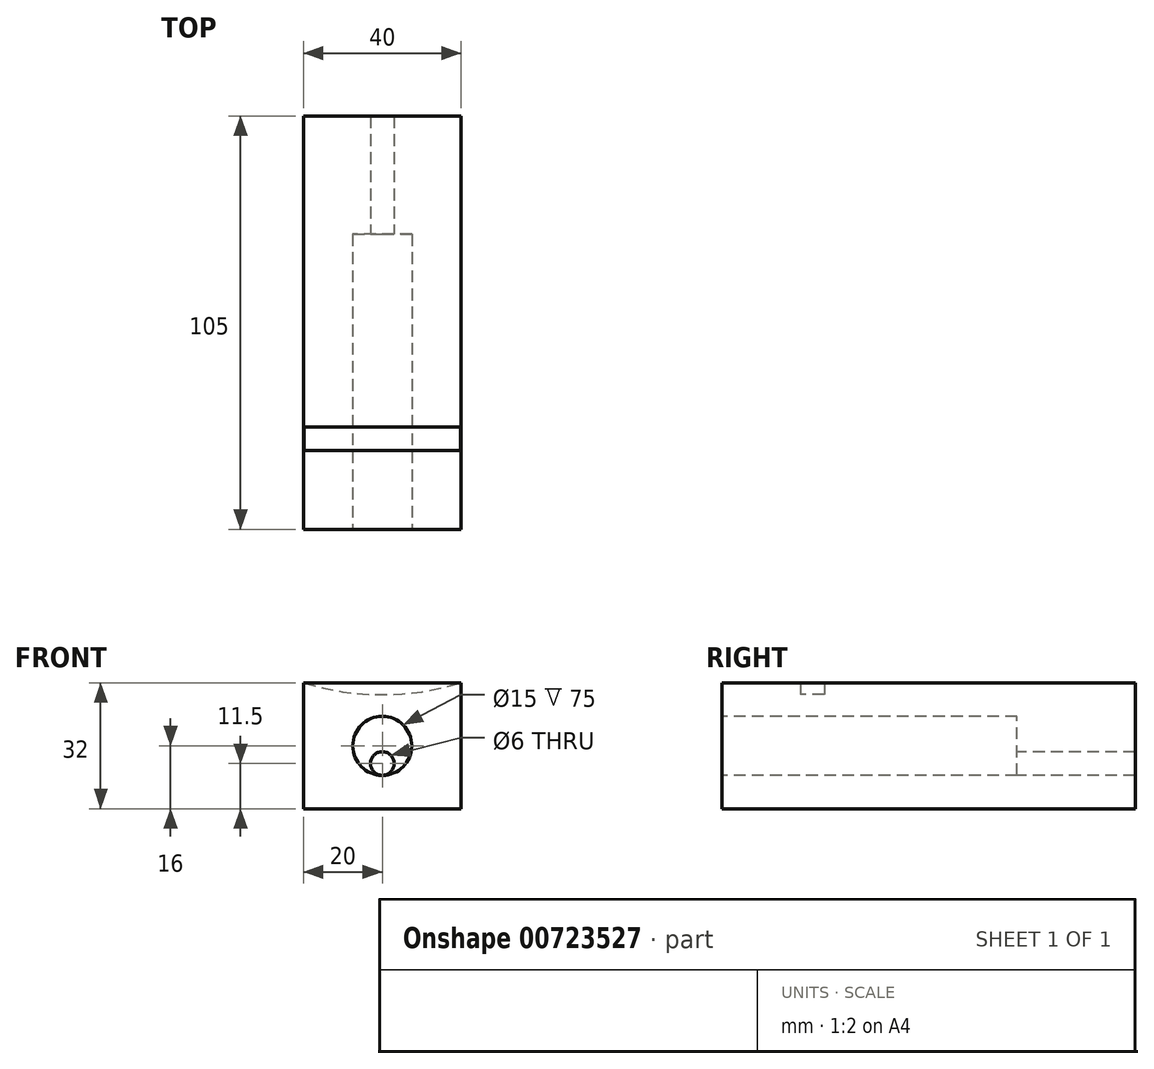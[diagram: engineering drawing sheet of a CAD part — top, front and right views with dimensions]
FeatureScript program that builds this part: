
annotation { "Feature Type Name" : "Feature", "Feature Type Description" : "" }
export const myFeature = defineFeature(function(context is Context, id is Id, definition is map)
    precondition{}
    {
        {
            var Q0;
            Q0=qCreatedBy(makeId("Front.planeOp"),FACE);
            var sketch = newSketch(context, id + "F0", { "sketchPlane" : qUnion([Q0])});
            skLineSegment(sketch, "E0.bottom", {"start": v(0, 0) * mm, "end": v(-40, 0) * mm});
            skLineSegment(sketch, "E0.top", {"start": v(0, 32) * mm, "end": v(-40, 32) * mm});
            skLineSegment(sketch, "E0.left", {"start": v(0, 0) * mm, "end": v(0, 32) * mm});
            skLineSegment(sketch, "E0.right", {"start": v(-40, 0) * mm, "end": v(-40, 32) * mm});
            skSolve(sketch);
        }
        {
            var Q0;
            Q0 = qSketchRegion(id + "F0", true);
            extrude(context, id + "F1", {"entities" : qUnion([Q0]), "oppositeDirection" : true, "depth" : 105 * mm, "offsetDistance" : 25 * mm});
        }
        {
            var Q0;
            Q0=makeQuery(id+"F1.opExtrude","CAP_FACE",FACE,{"disambiguationData":[OSD([sQuery(id+"F0.wireOp",EDGE,"E0.bottom"),sQuery(id+"F0.wireOp",EDGE,"E0.top"),sQuery(id+"F0.wireOp",EDGE,"E0.left"),sQuery(id+"F0.wireOp",EDGE,"E0.right")])],"isStart":true});
            var sketch = newSketch(context, id + "F2", { "sketchPlane" : qUnion([Q0])});
            skCircle(sketch, "E1", {"center": v(-20, 16) * mm, "radius": 7.5 * mm});
            skPoint(sketch, "E1.centerSnap0", {"position": v(0, 16) * mm});
            skPoint(sketch, "E1.centerSnap1", {"position": v(-20, 0) * mm});
            skSolve(sketch);
        }
        {
            var Q0;
            Q0 = qSketchRegion(id + "F2", true);
            extrude(context, id + "F3", {"entities" : qUnion([Q0]), "operationType" : NewBodyOperationType.REMOVE, "oppositeDirection" : true, "depth" : 75 * mm, "offsetDistance" : 25 * mm});
        }
        {
            var Q0;
            Q0=qCreatedBy(makeId("Front.planeOp"),FACE);
            var sketch = newSketch(context, id + "F4", { "sketchPlane" : qUnion([Q0])});
            skLineSegment(sketch, "E2", {"start": v(0, 0) * mm, "end": v(-20, 0) * mm, "construction": true});
            skLineSegment(sketch, "E3", {"start": v(-20, 0) * mm, "end": v(-20, 16) * mm, "construction": true});
            skLineSegment(sketch, "E4", {"start": v(-20, 16) * mm, "end": v(-20, 8.5) * mm, "construction": true});
            skLineSegment(sketch, "E5", {"start": v(-20, 8.5) * mm, "end": v(-20, 11.5) * mm, "construction": true});
            skCircle(sketch, "E6", {"center": v(-20, 11.5) * mm, "radius": 3 * mm});
            skSolve(sketch);
        }
        {
            var Q0;
            Q0 = qSketchRegion(id + "F4", true);
            extrude(context, id + "F5", {"entities" : qUnion([Q0]), "operationType" : NewBodyOperationType.REMOVE, "endBound" : BoundingType.THROUGH_ALL, "oppositeDirection" : true, "depth" : 25 * mm, "offsetDistance" : 25 * mm});
        }
        {
            var Q0;
            Q0=qCreatedBy(makeId("Front.planeOp"),FACE);
            cPlane(context, id + "F6", {"entities" : qUnion([Q0]), "cplaneType" : CPlaneType.OFFSET, "offset" : 20 * mm, "oppositeDirection" : true, "width" : 150 * mm, "height" : 150 * mm});
        }
        {
            var Q0;
            Q0=qCreatedBy(id+"F6.planeOp",FACE);
            var sketch = newSketch(context, id + "F7", { "sketchPlane" : qUnion([Q0])});
            skLineSegment(sketch, "E7", {"start": v(0, 0) * mm, "end": v(0, 32) * mm, "construction": true});
            skLineSegment(sketch, "E8", {"start": v(0, 32) * mm, "end": v(-40, 32) * mm, "construction": true});
            skLineSegment(sketch, "E9", {"start": v(-40, 32) * mm, "end": v(-40, 29) * mm, "construction": true});
            skLineSegment(sketch, "E10", {"start": v(-40, 29) * mm, "end": v(0, 29) * mm, "construction": true});
            skLineSegment(sketch, "E11", {"start": v(-20, 29) * mm, "end": v(-20, 164) * mm, "construction": true});
            skCircle(sketch, "E12", {"center": v(-20, 96.5) * mm, "radius": 67.5 * mm});
            skSolve(sketch);
        }
        {
            var Q0;
            Q0 = qSketchRegion(id + "F7", true);
            extrude(context, id + "F8", {"entities" : qUnion([Q0]), "operationType" : NewBodyOperationType.REMOVE, "oppositeDirection" : true, "depth" : 6 * mm, "offsetDistance" : 25 * mm});
        }
    });
